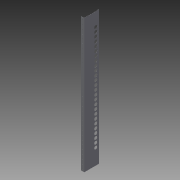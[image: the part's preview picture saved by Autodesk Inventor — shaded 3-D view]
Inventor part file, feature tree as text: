
AUTODESK INVENTOR PART (.ipt)
format: ipt  version: 2014 (Build 180170000, 170)  size: 159,232 bytes
history: native  units: in
note: dims shown in document units (in); Inventor stores cm internally (conversion verified against a paired STEP export)
features: sketch x3, hole x2, pattern_linear x2, extrude x1
ambient origin geometry x8: Origin, YZ Plane, XZ Plane, XY Plane, X Axis, Y Axis, Z Axis, Center Point
bodies: Solid1 (feature_tree)
feature tree (8):
  extrude  "Extrusion1"  Depth=0.75in
  hole  "Hole1"  [1 undecoded]
  pattern_linear  "Rectangular Pattern1"  Spacing1=0.25in  [1 undecoded]
  sketch  "Sketch3"  dims[d5=32.0in d6=0.0in d7=0.25in d8=0.5in d9=0.1in d10=0.75in d11=0.375in d12=0.25in d13=0.5635in d14=0.12in d15=0.8108in d16=12.5984in d18=1.0in d19=0.75in d20=3.75in d21=0.75in d22=0.75in d23=0.375in d24=0.25in d25=0.5635in d26=0.12in d27=0.8108in d28=10.2362in d30=1.0in]
  hole  "Hole2"  [1 undecoded]
  pattern_linear  "Rectangular Pattern2"  Spacing1=0.8108in  [1 undecoded]
  sketch  "Sketch1"  dims[d0=3.5in d1=0.75in]
  sketch  "Sketch2"  dims[d2=0.025in d4=0.025in]
note: 4 required parameter values undecoded (feature->parameter linkage not recoverable at this tier; creation-order binding heuristic only, values carry confidence <= 0.55)
